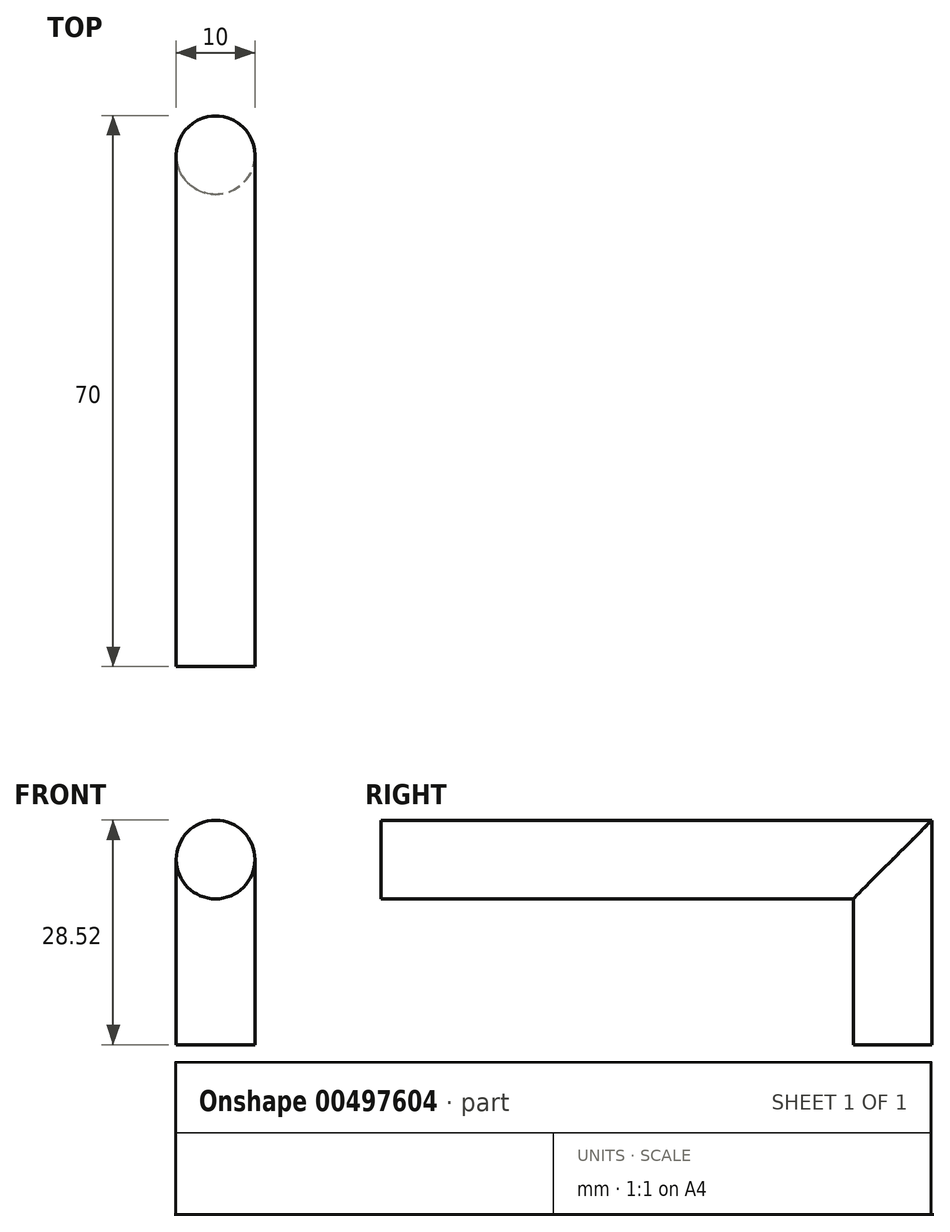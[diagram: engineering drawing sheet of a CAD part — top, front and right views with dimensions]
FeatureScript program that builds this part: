
annotation { "Feature Type Name" : "Feature", "Feature Type Description" : "" }
export const myFeature = defineFeature(function(context is Context, id is Id, definition is map)
    precondition{}
    {
        {
            var Q0;
            Q0=qCreatedBy(makeId("Right.planeOp"),FACE);
            var sketch = newSketch(context, id + "F0", { "sketchPlane" : qUnion([Q0])});
            skLineSegment(sketch, "E0", {"start": v(0, 0) * mm, "end": v(0, 18.52) * mm});
            skLineSegment(sketch, "E1", {"start": v(0, 18.52) * mm, "end": v(-60, 18.52) * mm});
            skLineSegment(sketch, "E2", {"start": v(-60, 18.52) * mm, "end": v(-60, 28.52) * mm});
            skLineSegment(sketch, "E3", {"start": v(-60, 28.52) * mm, "end": v(10, 28.52) * mm});
            skLineSegment(sketch, "E4", {"start": v(10, 28.52) * mm, "end": v(10, 0) * mm});
            skLineSegment(sketch, "E5", {"start": v(10, 0) * mm, "end": v(0, 0) * mm});
            skSolve(sketch);
        }
        {
            var Q0;
            Q0 = qSketchRegion(id + "F0", true);
            extrude(context, id + "F1", {"entities" : qUnion([Q0]), "depth" : 10 * mm});
        }
        {
            var Q0;
            Q0=makeQuery(id+"F1.opExtrude","CAP_EDGE",EDGE,{"disambiguationData":[OSD([sQuery(id+"F0.wireOp",EDGE,"E1")])],"isStart":false});
            var Q1;
            Q1=makeQuery(id+"F1.opExtrude","CAP_EDGE",EDGE,{"disambiguationData":[OSD([sQuery(id+"F0.wireOp",EDGE,"E1")])],"isStart":true});
            var Q2;
            Q2=makeQuery(id+"F1.opExtrude","CAP_EDGE",EDGE,{"disambiguationData":[OSD([sQuery(id+"F0.wireOp",EDGE,"E3")])],"isStart":false});
            var Q3;
            Q3=makeQuery(id+"F1.opExtrude","CAP_EDGE",EDGE,{"disambiguationData":[OSD([sQuery(id+"F0.wireOp",EDGE,"E3")])],"isStart":true});
            var Q4;
            Q4=makeQuery(id+"F1.opExtrude","CAP_EDGE",EDGE,{"disambiguationData":[OSD([sQuery(id+"F0.wireOp",EDGE,"E0")])],"isStart":false});
            var Q5;
            Q5=makeQuery(id+"F1.opExtrude","CAP_EDGE",EDGE,{"disambiguationData":[OSD([sQuery(id+"F0.wireOp",EDGE,"E0")])],"isStart":true});
            var Q6;
            Q6=makeQuery(id+"F1.opExtrude","CAP_EDGE",EDGE,{"disambiguationData":[OSD([sQuery(id+"F0.wireOp",EDGE,"E4")])],"isStart":true});
            var Q7;
            Q7=makeQuery(id+"F1.opExtrude","CAP_EDGE",EDGE,{"disambiguationData":[OSD([sQuery(id+"F0.wireOp",EDGE,"E4")])],"isStart":false});
            fillet(context, id + "F2", {"entities" : qUnion([Q0, Q1, Q2, Q3, Q4, Q5, Q6, Q7]), "radius" : 5 * mm, "tangentPropagation" : true, "allowEdgeOverflow" : false});
        }
    });
